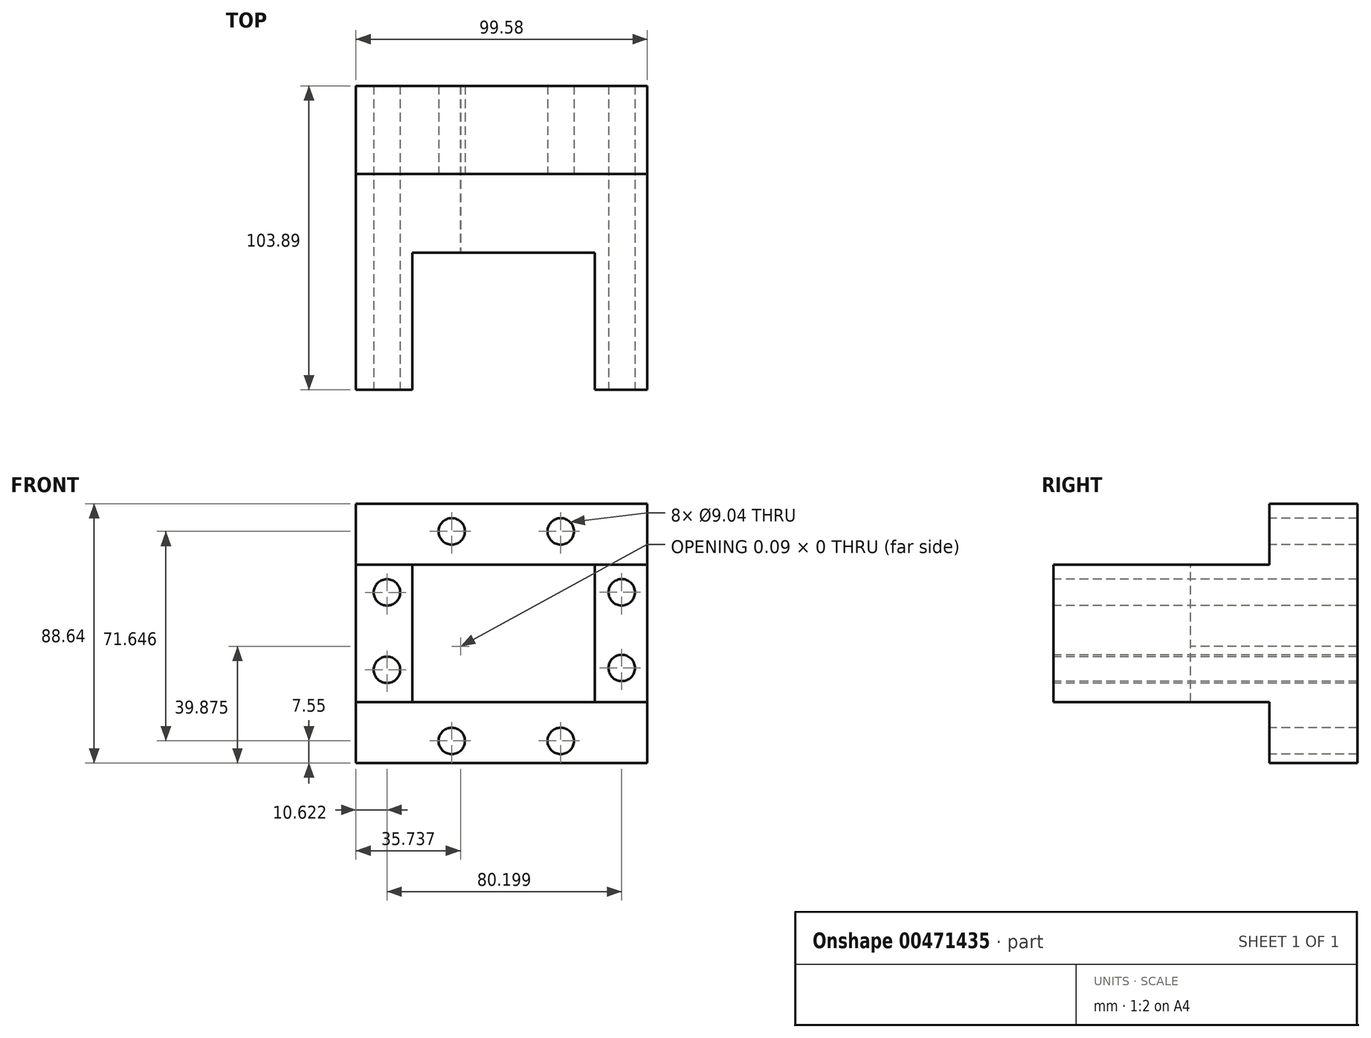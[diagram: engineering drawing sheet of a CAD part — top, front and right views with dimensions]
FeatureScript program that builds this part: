
annotation { "Feature Type Name" : "Feature", "Feature Type Description" : "" }
export const myFeature = defineFeature(function(context is Context, id is Id, definition is map)
    precondition{}
    {
        {
            var Q0;
            Q0=qCreatedBy(makeId("Front.planeOp"),FACE);
            var sketch = newSketch(context, id + "F0", { "sketchPlane" : qUnion([Q0])});
            skLineSegment(sketch, "E0.bottom", {"start": v(49.8, 44.32) * mm, "end": v(-49.8, 44.32) * mm});
            skLineSegment(sketch, "E0.top", {"start": v(49.8, -44.32) * mm, "end": v(-49.8, -44.32) * mm});
            skLineSegment(sketch, "E0.left", {"start": v(49.8, 44.32) * mm, "end": v(49.8, -44.32) * mm});
            skLineSegment(sketch, "E0.right", {"start": v(-49.8, 44.32) * mm, "end": v(-49.8, -44.32) * mm});
            skPoint(sketch, "E0.middle", {"position": v(0, 0) * mm});
            skSolve(sketch);
        }
        {
            var Q0;
            Q0 = qSketchRegion(id + "F0", true);
            extrude(context, id + "F1", {"entities" : qUnion([Q0]), "oppositeDirection" : true, "depth" : 103.89 * mm});
        }
        {
            var Q0;
            Q0=makeQuery(id+"F1.opExtrude","SWEPT_FACE",FACE,{"disambiguationData":[OSD([sQuery(id+"F0.wireOp",EDGE,"E0.left")])]});
            var sketch = newSketch(context, id + "F2", { "sketchPlane" : qUnion([Q0])});
            skLineSegment(sketch, "E1.bottom", {"start": v(0, 44.32) * mm, "end": v(73.81, 44.32) * mm});
            skLineSegment(sketch, "E1.top", {"start": v(0, 23.51) * mm, "end": v(73.81, 23.51) * mm});
            skLineSegment(sketch, "E1.left", {"start": v(0, 44.32) * mm, "end": v(0, 23.51) * mm});
            skLineSegment(sketch, "E1.right", {"start": v(73.81, 44.32) * mm, "end": v(73.81, 23.51) * mm});
            skLineSegment(sketch, "E2.bottom", {"start": v(0, -44.32) * mm, "end": v(73.81, -44.32) * mm});
            skLineSegment(sketch, "E2.top", {"start": v(0, -23.51) * mm, "end": v(73.81, -23.51) * mm});
            skLineSegment(sketch, "E2.left", {"start": v(0, -44.32) * mm, "end": v(0, -23.51) * mm});
            skLineSegment(sketch, "E2.right", {"start": v(73.81, -44.32) * mm, "end": v(73.81, -23.51) * mm});
            skSolve(sketch);
        }
        {
            var Q0;
            Q0 = qSketchRegion(id + "F2", true);
            extrude(context, id + "F3", {"entities" : qUnion([Q0]), "operationType" : NewBodyOperationType.REMOVE, "oppositeDirection" : true, "depth" : 202.18 * mm});
        }
        {
            var Q0;
            Q0=qCreatedBy(makeId("Front.planeOp"),FACE);
            var sketch = newSketch(context, id + "F4", { "sketchPlane" : qUnion([Q0])});
            skCircle(sketch, "E3", {"center": v(-17.04, 34.88) * mm, "radius": 4.52 * mm});
            skCircle(sketch, "E4", {"center": v(20.2, 34.88) * mm, "radius": 4.52 * mm});
            skCircle(sketch, "E5", {"center": v(-17.04, -36.77) * mm, "radius": 4.52 * mm});
            skCircle(sketch, "E6", {"center": v(20.2, -36.77) * mm, "radius": 4.52 * mm});
            skCircle(sketch, "E7", {"center": v(-39.17, 14) * mm, "radius": 4.52 * mm});
            skCircle(sketch, "E8", {"center": v(-39.17, -12.47) * mm, "radius": 4.52 * mm});
            skCircle(sketch, "E9", {"center": v(41.03, 14.05) * mm, "radius": 4.52 * mm});
            skCircle(sketch, "E10", {"center": v(41.03, -11.84) * mm, "radius": 4.52 * mm});
            skSolve(sketch);
        }
        {
            var Q0;
            Q0 = qSketchRegion(id + "F4", true);
            extrude(context, id + "F5", {"entities" : qUnion([Q0]), "operationType" : NewBodyOperationType.REMOVE, "oppositeDirection" : true, "depth" : 183.39 * mm});
        }
        {
            var Q0;
            Q0=makeQuery(id+"F3.boolean.opBoolean","COPY",FACE,{"derivedFrom":makeQuery(id+"F3.opExtrude","SWEPT_FACE",FACE,{"disambiguationData":[OSD([sQuery(id+"F2.wireOp",EDGE,"E1.top")])]})});
            var sketch = newSketch(context, id + "F6", { "sketchPlane" : qUnion([Q0])});
            skLineSegment(sketch, "E11.bottom", {"start": v(-30.46, 0) * mm, "end": v(31.8, 0) * mm});
            skLineSegment(sketch, "E11.top", {"start": v(-30.46, 46.83) * mm, "end": v(31.8, 46.83) * mm});
            skLineSegment(sketch, "E11.left", {"start": v(-30.46, 0) * mm, "end": v(-30.46, 46.83) * mm});
            skLineSegment(sketch, "E11.right", {"start": v(31.8, 0) * mm, "end": v(31.8, 46.83) * mm});
            skSolve(sketch);
        }
        {
            var Q0;
            Q0 = qSketchRegion(id + "F6", true);
            extrude(context, id + "F7", {"entities" : qUnion([Q0]), "operationType" : NewBodyOperationType.REMOVE, "oppositeDirection" : true, "depth" : 52.07 * mm});
        }
        {
            var Q0;
            Q0=makeQuery(id+"F7.boolean.opBoolean","COPY",FACE,{"derivedFrom":makeQuery(id+"F7.opExtrude","SWEPT_FACE",FACE,{"disambiguationData":[OSD([sQuery(id+"F6.wireOp",EDGE,"E11.top")])]})});
            var sketch = newSketch(context, id + "F8", { "sketchPlane" : qUnion([Q0])});
            skArc(sketch, "E12", {"start": v(-14.78, 4.38) * mm, "mid": v(-18.48, -0.39) * mm, "end": v(-14, -4.44) * mm});
            skArc(sketch, "E13", {"start": v(13.89, -4.44) * mm, "mid": v(18.32, 0.37) * mm, "end": v(13.16, 4.38) * mm});
            skArc(sketch, "E14", {"start": v(-4.45, -14.7) * mm, "mid": v(0, -19.15) * mm, "end": v(4.44, -14.7) * mm});
            skArc(sketch, "E15", {"start": v(4.44, 13.17) * mm, "mid": v(0.03, 17.68) * mm, "end": v(-4.45, 13.24) * mm});
            skLineSegment(sketch, "E16", {"start": v(-14.78, 4.38) * mm, "end": v(-4.45, 4.38) * mm});
            skLineSegment(sketch, "E17", {"start": v(-14.1, -4.44) * mm, "end": v(-4.45, -4.44) * mm});
            skLineSegment(sketch, "E18", {"start": v(-4.45, 13.24) * mm, "end": v(-4.45, 4.38) * mm});
            skLineSegment(sketch, "E19", {"start": v(4.44, 13.17) * mm, "end": v(4.44, 4.38) * mm});
            skLineSegment(sketch, "E20.trimOffspring", {"start": v(4.44, -4.44) * mm, "end": v(4.44, -14.7) * mm});
            skLineSegment(sketch, "E21.trimOffspring", {"start": v(-4.45, -4.44) * mm, "end": v(-4.45, -14.7) * mm});
            skLineSegment(sketch, "E22.trimOffspring", {"start": v(4.44, 4.38) * mm, "end": v(13.16, 4.38) * mm});
            skLineSegment(sketch, "E23.trimOffspring", {"start": v(4.44, -4.44) * mm, "end": v(13.89, -4.44) * mm});
            skSolve(sketch);
        }
        {
            var Q0;
            {var subQ3=sQuery(id+"F8.wireOp",EDGE,"E12");Q0=makeQuery(id+"F8.imprint","IMPRINT",FACE,{"disambiguationData":[TD([[makeQuery(id+"F8.imprint","IMPRINT",EDGE,{"derivedFrom":subQ3}),1.0]])]});}
            extrude(context, id + "F9", {"entities" : qUnion([Q0]), "operationType" : NewBodyOperationType.REMOVE, "oppositeDirection" : true, "depth" : 124.46 * mm});
        }
    });
